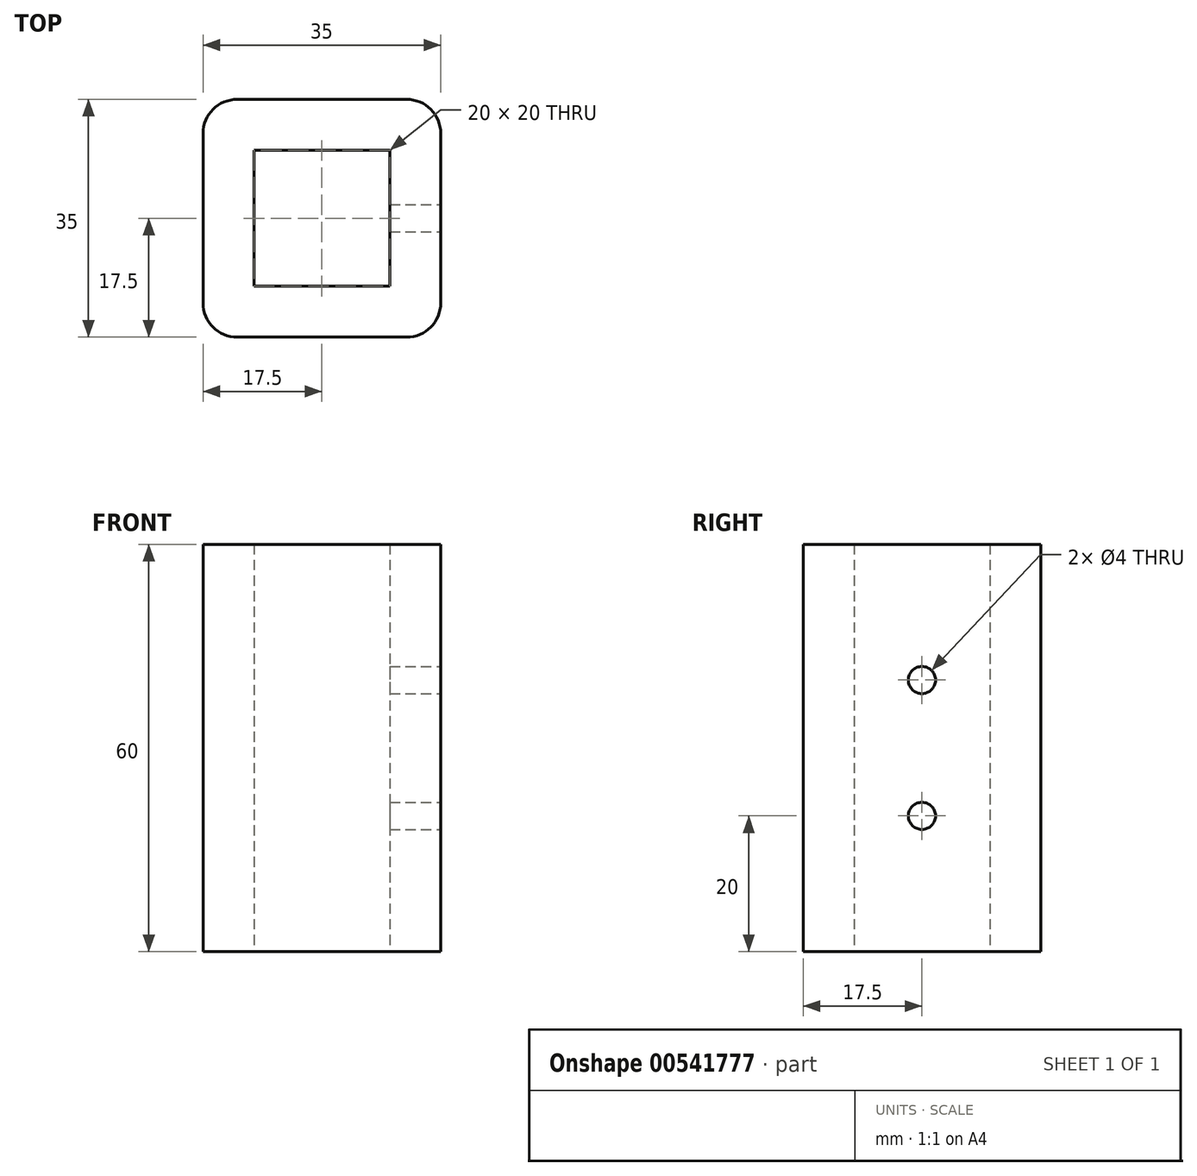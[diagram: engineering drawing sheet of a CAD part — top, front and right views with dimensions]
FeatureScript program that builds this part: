
annotation { "Feature Type Name" : "Feature", "Feature Type Description" : "" }
export const myFeature = defineFeature(function(context is Context, id is Id, definition is map)
    precondition{}
    {
        {
            var Q0;
            Q0=qCreatedBy(makeId("Top.planeOp"),FACE);
            var sketch = newSketch(context, id + "F0", { "sketchPlane" : qUnion([Q0])});
            skLineSegment(sketch, "E0.bottom", {"start": v(-17.5, -17.5) * mm, "end": v(17.5, -17.5) * mm});
            skLineSegment(sketch, "E0.top", {"start": v(-17.5, 17.5) * mm, "end": v(17.5, 17.5) * mm});
            skLineSegment(sketch, "E0.left", {"start": v(-17.5, -17.5) * mm, "end": v(-17.5, 17.5) * mm});
            skLineSegment(sketch, "E0.right", {"start": v(17.5, -17.5) * mm, "end": v(17.5, 17.5) * mm});
            skLineSegment(sketch, "E1.bottom", {"start": v(-10, -10) * mm, "end": v(10, -10) * mm});
            skLineSegment(sketch, "E1.top", {"start": v(-10, 10) * mm, "end": v(10, 10) * mm});
            skLineSegment(sketch, "E1.left", {"start": v(-10, -10) * mm, "end": v(-10, 10) * mm});
            skLineSegment(sketch, "E1.right", {"start": v(10, -10) * mm, "end": v(10, 10) * mm});
            skPoint(sketch, "E2", {"position": v(0, 10) * mm});
            skPoint(sketch, "E3", {"position": v(0, 17.5) * mm});
            skPoint(sketch, "E4", {"position": v(-17.5, 0) * mm});
            skPoint(sketch, "E5", {"position": v(-10, 0) * mm});
            skSolve(sketch);
        }
        {
            var Q0;
            Q0=makeQuery(id+"F0.imprint","IMPRINT",FACE,{"disambiguationData":[TD([[makeQuery(id+"F0.imprint","IMPRINT",EDGE,{"derivedFrom":sQuery(id+"F0.wireOp",EDGE,"E0.bottom")}),1.0]])]});
            extrude(context, id + "F1", {"entities" : qUnion([Q0]), "depth" : 60 * mm, "offsetDistance" : 25 * mm});
        }
        {
            var Q0;
            Q0=makeQuery(id+"F1.opExtrude","SWEPT_EDGE",EDGE,{"disambiguationData":[OSD([sQuery(id+"F0.wireOp",EDGE,"E0.top"),sQuery(id+"F0.wireOp",EDGE,"E0.right")])]});
            var Q1;
            Q1=makeQuery(id+"F1.opExtrude","SWEPT_EDGE",EDGE,{"disambiguationData":[OSD([sQuery(id+"F0.wireOp",EDGE,"E0.top"),sQuery(id+"F0.wireOp",EDGE,"E0.left")])]});
            var Q2;
            Q2=makeQuery(id+"F1.opExtrude","SWEPT_EDGE",EDGE,{"disambiguationData":[OSD([sQuery(id+"F0.wireOp",EDGE,"E0.bottom"),sQuery(id+"F0.wireOp",EDGE,"E0.right")])]});
            var Q3;
            Q3=makeQuery(id+"F1.opExtrude","SWEPT_EDGE",EDGE,{"disambiguationData":[OSD([sQuery(id+"F0.wireOp",EDGE,"E0.bottom"),sQuery(id+"F0.wireOp",EDGE,"E0.left")])]});
            fillet(context, id + "F2", {"entities" : qUnion([Q0, Q1, Q2, Q3]), "radius" : 5 * mm, "tangentPropagation" : true, "allowEdgeOverflow" : false});
        }
        {
            var Q0;
            Q0=makeQuery(id+"F1.opExtrude","SWEPT_FACE",FACE,{"disambiguationData":[OSD([sQuery(id+"F0.wireOp",EDGE,"E0.right")])]});
            var sketch = newSketch(context, id + "F3", { "sketchPlane" : qUnion([Q0])});
            skCircle(sketch, "E6", {"center": v(0, 40) * mm, "radius": 2 * mm});
            skCircle(sketch, "E7", {"center": v(0, 20) * mm, "radius": 2 * mm});
            skSolve(sketch);
        }
        {
            var Q0;
            Q0 = qSketchRegion(id + "F3", true);
            extrude(context, id + "F4", {"entities" : qUnion([Q0]), "operationType" : NewBodyOperationType.REMOVE, "oppositeDirection" : true, "depth" : 10 * mm, "offsetDistance" : 25 * mm});
        }
    });
